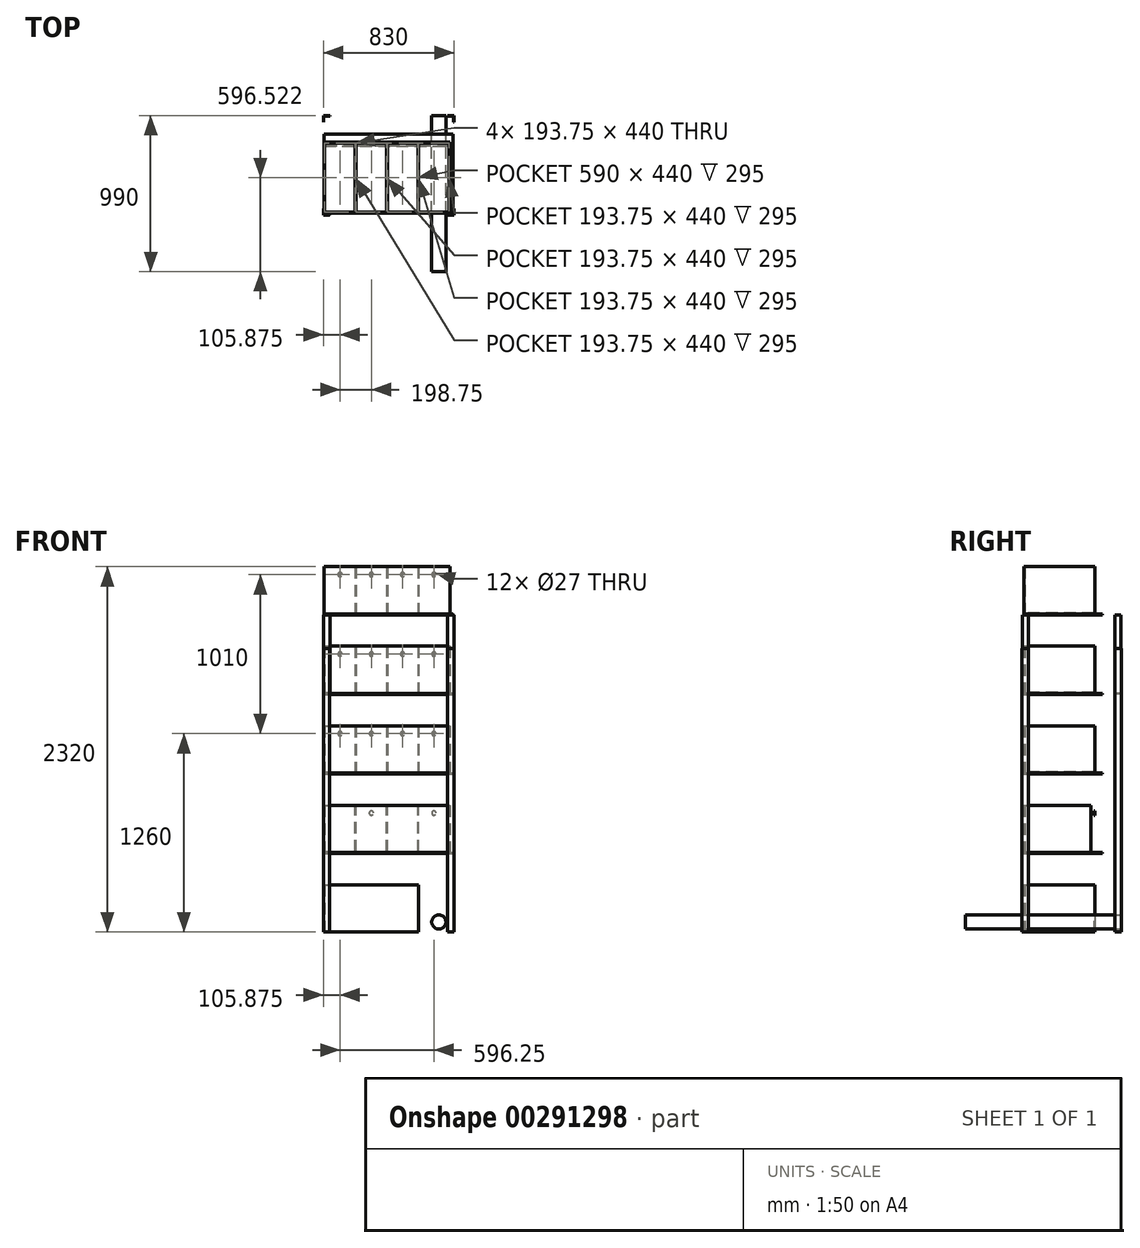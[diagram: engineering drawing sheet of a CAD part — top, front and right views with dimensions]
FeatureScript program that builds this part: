
annotation { "Feature Type Name" : "Feature", "Feature Type Description" : "" }
export const myFeature = defineFeature(function(context is Context, id is Id, definition is map)
    precondition{}
    {
        {
            var Q0;
            Q0=qCreatedBy(makeId("Top.planeOp"),FACE);
            var sketch = newSketch(context, id + "F0", { "sketchPlane" : qUnion([Q0])});
            skLineSegment(sketch, "E0.bottom", {"start": v(-415, 315) * mm, "end": v(415, 315) * mm});
            skLineSegment(sketch, "E0.top", {"start": v(-415, -315) * mm, "end": v(415, -315) * mm});
            skLineSegment(sketch, "E0.left", {"start": v(-415, 315) * mm, "end": v(-415, -315) * mm});
            skLineSegment(sketch, "E0.right", {"start": v(415, 315) * mm, "end": v(415, -315) * mm});
            skPoint(sketch, "E0.middle", {"position": v(0, 0) * mm});
            skSolve(sketch);
        }
        {
            var Q0;
            Q0=qCreatedBy(makeId("Top.planeOp"),FACE);
            var sketch = newSketch(context, id + "F1", { "sketchPlane" : qUnion([Q0])});
            skLineSegment(sketch, "E1.bottom", {"start": v(-411, -303.48) * mm, "end": v(409, -303.48) * mm});
            skLineSegment(sketch, "E1.top", {"start": v(-411, 196.52) * mm, "end": v(409, 196.52) * mm});
            skLineSegment(sketch, "E1.left", {"start": v(-411, -303.48) * mm, "end": v(-411, 196.52) * mm});
            skLineSegment(sketch, "E1.right", {"start": v(409, -303.48) * mm, "end": v(409, 196.52) * mm});
            skSolve(sketch);
        }
        {
            var Q0;
            Q0=qCreatedBy(makeId("Top.planeOp"),FACE);
            var sketch = newSketch(context, id + "F2", { "sketchPlane" : qUnion([Q0])});
            skPoint(sketch, "E2.0", {"position": v(-411, -303.48) * mm});
            skLineSegment(sketch, "E3.bottom", {"start": v(-411, -303.48) * mm, "end": v(189, -303.48) * mm});
            skLineSegment(sketch, "E3.top", {"start": v(-411, 146.52) * mm, "end": v(189, 146.52) * mm});
            skLineSegment(sketch, "E3.left", {"start": v(-411, -303.48) * mm, "end": v(-411, 146.52) * mm});
            skLineSegment(sketch, "E3.right", {"start": v(189, -303.48) * mm, "end": v(189, 146.52) * mm});
            skSolve(sketch);
        }
        {
            var Q0;
            Q0 = qSketchRegion(id + "F2", true);
            extrude(context, id + "F3", {"entities" : qUnion([Q0]), "depth" : 300 * mm});
        }
        {
            var Q0;
            Q0=qCreatedBy(makeId("Top.planeOp"),FACE);
            cPlane(context, id + "F4", {"entities" : qUnion([Q0]), "cplaneType" : CPlaneType.OFFSET, "offset" : 500 * mm, "width" : 150 * mm, "height" : 150 * mm});
        }
        {
            var Q0;
            Q0=qCreatedBy(id+"F4.planeOp",FACE);
            var sketch = newSketch(context, id + "F5", { "sketchPlane" : qUnion([Q0])});
            skLineSegment(sketch, "E4.0", {"start": v(-411, 196.52) * mm, "end": v(409, 196.52) * mm});
            skLineSegment(sketch, "E5.0", {"start": v(-411, -303.48) * mm, "end": v(-411, 196.52) * mm});
            skPoint(sketch, "E6.0", {"position": v(409, -303.48) * mm});
            skLineSegment(sketch, "E7.top", {"start": v(-411, -303.48) * mm, "end": v(409, -303.48) * mm});
            skLineSegment(sketch, "E7.left", {"start": v(-411, 196.52) * mm, "end": v(-411, -303.48) * mm});
            skLineSegment(sketch, "E7.right", {"start": v(409, 196.52) * mm, "end": v(409, -303.48) * mm});
            skSolve(sketch);
        }
        {
            var Q0;
            Q0 = qSketchRegion(id + "F5", true);
            extrude(context, id + "F6", {"entities" : qUnion([Q0]), "depth" : 5 * mm});
        }
        {
            var Q0;
            Q0=makeQuery(id+"F6.opExtrude","CAP_FACE",FACE,{"disambiguationData":[OSD([sQuery(id+"F5.wireOp",EDGE,"E4.0"),sQuery(id+"F5.wireOp",EDGE,"E7.top"),sQuery(id+"F5.wireOp",EDGE,"E7.left"),sQuery(id+"F5.wireOp",EDGE,"E7.right")])],"isStart":false});
            var sketch = newSketch(context, id + "F7", { "sketchPlane" : qUnion([Q0])});
            skPoint(sketch, "E8.0", {"position": v(-411, -303.48) * mm});
            skLineSegment(sketch, "E9.bottom", {"start": v(-411, -303.48) * mm, "end": v(389, -303.48) * mm});
            skLineSegment(sketch, "E9.top", {"start": v(-411, 146.52) * mm, "end": v(389, 146.52) * mm});
            skLineSegment(sketch, "E9.left", {"start": v(-411, -303.48) * mm, "end": v(-411, 146.52) * mm});
            skLineSegment(sketch, "E9.right", {"start": v(389, -303.48) * mm, "end": v(389, 146.52) * mm});
            skSolve(sketch);
        }
        {
            var Q0;
            Q0=makeQuery(id+"F7.imprint","IMPRINT",FACE,{"disambiguationData":[TD([[makeQuery(id+"F7.imprint","IMPRINT",EDGE,{"derivedFrom":sQuery(id+"F7.wireOp",EDGE,"E9.bottom")}),1.0]])]});
            extrude(context, id + "F8", {"entities" : qUnion([Q0]), "depth" : 300 * mm});
        }
        {
            var Q0;
            Q0=makeQuery(id+"F8.opExtrude","CAP_FACE",FACE,{"disambiguationData":[OSD([sQuery(id+"F7.wireOp",EDGE,"E9.bottom"),sQuery(id+"F7.wireOp",EDGE,"E9.top"),sQuery(id+"F7.wireOp",EDGE,"E9.left"),sQuery(id+"F7.wireOp",EDGE,"E9.right")])],"isStart":false});
            shell(context, id + "F9", {"entities" : qUnion([Q0]), "thickness" : 5 * mm});
        }
        {
            var Q0;
            Q0=makeQuery(id+"F6.opExtrude","CAP_FACE",FACE,{"disambiguationData":[OSD([sQuery(id+"F5.wireOp",EDGE,"E4.0"),sQuery(id+"F5.wireOp",EDGE,"E7.top"),sQuery(id+"F5.wireOp",EDGE,"E7.left"),sQuery(id+"F5.wireOp",EDGE,"E7.right")])],"isStart":false});
            cPlane(context, id + "F10", {"entities" : qUnion([Q0]), "cplaneType" : CPlaneType.OFFSET, "offset" : 500 * mm, "width" : 150 * mm, "height" : 150 * mm});
        }
        {
            var Q0;
            Q0=qCreatedBy(id+"F10.planeOp",FACE);
            var sketch = newSketch(context, id + "F11", { "sketchPlane" : qUnion([Q0])});
            skPoint(sketch, "E10.0", {"position": v(-411, -303.48) * mm});
            skPoint(sketch, "E11.0", {"position": v(409, 196.52) * mm});
            skLineSegment(sketch, "E12.bottom", {"start": v(-411, -303.48) * mm, "end": v(409, -303.48) * mm});
            skLineSegment(sketch, "E12.top", {"start": v(-411, 196.52) * mm, "end": v(409, 196.52) * mm});
            skLineSegment(sketch, "E12.left", {"start": v(-411, -303.48) * mm, "end": v(-411, 196.52) * mm});
            skLineSegment(sketch, "E12.right", {"start": v(409, -303.48) * mm, "end": v(409, 196.52) * mm});
            skSolve(sketch);
        }
        {
            var Q0;
            Q0 = qSketchRegion(id + "F11", true);
            extrude(context, id + "F12", {"entities" : qUnion([Q0]), "depth" : 5 * mm});
        }
        {
            var Q0;
            Q0=makeQuery(id+"F12.opExtrude","CAP_FACE",FACE,{"disambiguationData":[OSD([sQuery(id+"F11.wireOp",EDGE,"E12.bottom"),sQuery(id+"F11.wireOp",EDGE,"E12.top"),sQuery(id+"F11.wireOp",EDGE,"E12.left"),sQuery(id+"F11.wireOp",EDGE,"E12.right")])],"isStart":false});
            var sketch = newSketch(context, id + "F13", { "sketchPlane" : qUnion([Q0])});
            skPoint(sketch, "E13.0", {"position": v(-411, -303.48) * mm});
            skLineSegment(sketch, "E14.bottom", {"start": v(-411, -303.48) * mm, "end": v(389, -303.48) * mm});
            skLineSegment(sketch, "E14.top", {"start": v(-411, 146.52) * mm, "end": v(389, 146.52) * mm});
            skLineSegment(sketch, "E14.left", {"start": v(-411, -303.48) * mm, "end": v(-411, 146.52) * mm});
            skLineSegment(sketch, "E14.right", {"start": v(389, -303.48) * mm, "end": v(389, 146.52) * mm});
            skSolve(sketch);
        }
        {
            var Q0;
            Q0=makeQuery(id+"F13.imprint","IMPRINT",FACE,{"disambiguationData":[TD([[makeQuery(id+"F13.imprint","IMPRINT",EDGE,{"derivedFrom":sQuery(id+"F13.wireOp",EDGE,"E14.bottom")}),1.0]])]});
            extrude(context, id + "F14", {"entities" : qUnion([Q0]), "depth" : 300 * mm});
        }
        {
            var Q0;
            Q0=makeQuery(id+"F14.opExtrude","CAP_FACE",FACE,{"disambiguationData":[OSD([sQuery(id+"F13.wireOp",EDGE,"E14.bottom"),sQuery(id+"F13.wireOp",EDGE,"E14.top"),sQuery(id+"F13.wireOp",EDGE,"E14.left"),sQuery(id+"F13.wireOp",EDGE,"E14.right")])],"isStart":false});
            shell(context, id + "F15", {"entities" : qUnion([Q0]), "thickness" : 5 * mm});
        }
        {
            var Q0;
            Q0=makeQuery(id+"F12.opExtrude","CAP_FACE",FACE,{"disambiguationData":[OSD([sQuery(id+"F11.wireOp",EDGE,"E12.bottom"),sQuery(id+"F11.wireOp",EDGE,"E12.top"),sQuery(id+"F11.wireOp",EDGE,"E12.left"),sQuery(id+"F11.wireOp",EDGE,"E12.right")])],"isStart":false});
            cPlane(context, id + "F16", {"entities" : qUnion([Q0]), "cplaneType" : CPlaneType.OFFSET, "offset" : 500 * mm, "width" : 150 * mm, "height" : 150 * mm});
        }
        {
            var Q0;
            Q0=qCreatedBy(id+"F16.planeOp",FACE);
            var sketch = newSketch(context, id + "F17", { "sketchPlane" : qUnion([Q0])});
            skPoint(sketch, "E15.0", {"position": v(-411, -303.48) * mm});
            skPoint(sketch, "E16.0", {"position": v(409, 196.52) * mm});
            skLineSegment(sketch, "E17.bottom", {"start": v(-411, -303.48) * mm, "end": v(409, -303.48) * mm});
            skLineSegment(sketch, "E17.top", {"start": v(-411, 196.52) * mm, "end": v(409, 196.52) * mm});
            skLineSegment(sketch, "E17.left", {"start": v(-411, -303.48) * mm, "end": v(-411, 196.52) * mm});
            skLineSegment(sketch, "E17.right", {"start": v(409, -303.48) * mm, "end": v(409, 196.52) * mm});
            skSolve(sketch);
        }
        {
            var Q0;
            Q0 = qSketchRegion(id + "F17", true);
            extrude(context, id + "F18", {"entities" : qUnion([Q0]), "depth" : 5 * mm});
        }
        {
            var Q0;
            Q0=makeQuery(id+"F18.opExtrude","CAP_FACE",FACE,{"disambiguationData":[OSD([sQuery(id+"F17.wireOp",EDGE,"E17.bottom"),sQuery(id+"F17.wireOp",EDGE,"E17.top"),sQuery(id+"F17.wireOp",EDGE,"E17.left"),sQuery(id+"F17.wireOp",EDGE,"E17.right")])],"isStart":false});
            var sketch = newSketch(context, id + "F19", { "sketchPlane" : qUnion([Q0])});
            skPoint(sketch, "E18.0", {"position": v(-411, -303.48) * mm});
            skLineSegment(sketch, "E19.bottom", {"start": v(-411, -303.48) * mm, "end": v(389, -303.48) * mm});
            skLineSegment(sketch, "E19.top", {"start": v(-411, 146.52) * mm, "end": v(389, 146.52) * mm});
            skLineSegment(sketch, "E19.left", {"start": v(-411, -303.48) * mm, "end": v(-411, 146.52) * mm});
            skLineSegment(sketch, "E19.right", {"start": v(389, -303.48) * mm, "end": v(389, 146.52) * mm});
            skSolve(sketch);
        }
        {
            var Q0;
            Q0=makeQuery(id+"F19.imprint","IMPRINT",FACE,{"disambiguationData":[TD([[makeQuery(id+"F19.imprint","IMPRINT",EDGE,{"derivedFrom":sQuery(id+"F19.wireOp",EDGE,"E19.bottom")}),1.0]])]});
            extrude(context, id + "F20", {"entities" : qUnion([Q0]), "depth" : 300 * mm});
        }
        {
            var Q0;
            Q0=makeQuery(id+"F20.opExtrude","CAP_FACE",FACE,{"disambiguationData":[OSD([sQuery(id+"F19.wireOp",EDGE,"E19.bottom"),sQuery(id+"F19.wireOp",EDGE,"E19.top"),sQuery(id+"F19.wireOp",EDGE,"E19.left"),sQuery(id+"F19.wireOp",EDGE,"E19.right")])],"isStart":false});
            shell(context, id + "F21", {"entities" : qUnion([Q0]), "thickness" : 5 * mm});
        }
        {
            var Q0;
            Q0=makeQuery(id+"F18.opExtrude","CAP_FACE",FACE,{"disambiguationData":[OSD([sQuery(id+"F17.wireOp",EDGE,"E17.bottom"),sQuery(id+"F17.wireOp",EDGE,"E17.top"),sQuery(id+"F17.wireOp",EDGE,"E17.left"),sQuery(id+"F17.wireOp",EDGE,"E17.right")])],"isStart":false});
            cPlane(context, id + "F22", {"entities" : qUnion([Q0]), "cplaneType" : CPlaneType.OFFSET, "offset" : 500 * mm, "width" : 150 * mm, "height" : 150 * mm});
        }
        {
            var Q0;
            Q0=qCreatedBy(id+"F22.planeOp",FACE);
            var sketch = newSketch(context, id + "F23", { "sketchPlane" : qUnion([Q0])});
            skPoint(sketch, "E20.0", {"position": v(-411, -303.48) * mm});
            skPoint(sketch, "E21.0", {"position": v(409, 196.52) * mm});
            skLineSegment(sketch, "E22.bottom", {"start": v(-411, -303.48) * mm, "end": v(409, -303.48) * mm});
            skLineSegment(sketch, "E22.top", {"start": v(-411, 196.52) * mm, "end": v(409, 196.52) * mm});
            skLineSegment(sketch, "E22.left", {"start": v(-411, -303.48) * mm, "end": v(-411, 196.52) * mm});
            skLineSegment(sketch, "E22.right", {"start": v(409, -303.48) * mm, "end": v(409, 196.52) * mm});
            skSolve(sketch);
        }
        {
            var Q0;
            Q0=makeQuery(id+"F23.imprint","IMPRINT",FACE,{"disambiguationData":[TD([[makeQuery(id+"F23.imprint","IMPRINT",EDGE,{"derivedFrom":sQuery(id+"F23.wireOp",EDGE,"E22.bottom")}),1.0]])]});
            extrude(context, id + "F24", {"entities" : qUnion([Q0]), "depth" : 5 * mm});
        }
        {
            var Q0;
            Q0=makeQuery(id+"F24.opExtrude","CAP_FACE",FACE,{"disambiguationData":[OSD([sQuery(id+"F23.wireOp",EDGE,"E22.bottom"),sQuery(id+"F23.wireOp",EDGE,"E22.top"),sQuery(id+"F23.wireOp",EDGE,"E22.left"),sQuery(id+"F23.wireOp",EDGE,"E22.right")])],"isStart":false});
            var sketch = newSketch(context, id + "F25", { "sketchPlane" : qUnion([Q0])});
            skPoint(sketch, "E23.0", {"position": v(-411, -303.48) * mm});
            skLineSegment(sketch, "E24.bottom", {"start": v(-411, -303.48) * mm, "end": v(389, -303.48) * mm});
            skLineSegment(sketch, "E24.top", {"start": v(-411, 146.52) * mm, "end": v(389, 146.52) * mm});
            skLineSegment(sketch, "E24.left", {"start": v(-411, -303.48) * mm, "end": v(-411, 146.52) * mm});
            skLineSegment(sketch, "E24.right", {"start": v(389, -303.48) * mm, "end": v(389, 146.52) * mm});
            skSolve(sketch);
        }
        {
            var Q0;
            Q0=makeQuery(id+"F25.imprint","IMPRINT",FACE,{"disambiguationData":[TD([[makeQuery(id+"F25.imprint","IMPRINT",EDGE,{"derivedFrom":sQuery(id+"F25.wireOp",EDGE,"E24.bottom")}),1.0]])]});
            extrude(context, id + "F26", {"entities" : qUnion([Q0]), "depth" : 300 * mm});
        }
        {
            var Q0;
            Q0=makeQuery(id+"F26.opExtrude","CAP_FACE",FACE,{"disambiguationData":[OSD([sQuery(id+"F25.wireOp",EDGE,"E24.bottom"),sQuery(id+"F25.wireOp",EDGE,"E24.top"),sQuery(id+"F25.wireOp",EDGE,"E24.left"),sQuery(id+"F25.wireOp",EDGE,"E24.right")])],"isStart":false});
            shell(context, id + "F27", {"entities" : qUnion([Q0]), "thickness" : 5 * mm});
        }
        {
            var Q0;
            Q0=sQuery(id+"F0.wireOp",EDGE,"E0.bottom");
            var Q1;
            Q1=makeQuery(id+"F1.imprint","IMPRINT",FACE,{"disambiguationData":[TD([[makeQuery(id+"F1.imprint","IMPRINT",EDGE,{"derivedFrom":sQuery(id+"F1.wireOp",EDGE,"E1.bottom")}),1.0]])]});
            cPlane(context, id + "F28", {"entities" : qUnion([Q0, Q1]), "cplaneType" : CPlaneType.LINE_ANGLE, "offset" : 25 * mm, "angle" : 90 * degree, "oppositeDirection" : true, "width" : 150 * mm, "height" : 150 * mm});
        }
        {
            var Q0;
            Q0=qCreatedBy(id+"F28.planeOp",FACE);
            var sketch = newSketch(context, id + "F29", { "sketchPlane" : qUnion([Q0])});
            skCircle(sketch, "E25", {"center": v(318.2, 63.11) * mm, "radius": 45 * mm});
            skSolve(sketch);
        }
        {
            var Q0;
            Q0=makeQuery(id+"F29.imprint","IMPRINT",FACE,{"disambiguationData":[TD([[makeQuery(id+"F29.imprint","IMPRINT",EDGE,{"derivedFrom":sQuery(id+"F29.wireOp",EDGE,"E25")}),1.0]])]});
            extrude(context, id + "F30", {"entities" : qUnion([Q0]), "depth" : 990 * mm});
        }
        {
            var Q0;
            Q0=makeQuery(id+"F9.opShell","OFFSET_FACE",FACE,{"disambiguationData":[OSD([sQuery(id+"F7.wireOp",EDGE,"E9.bottom"),sQuery(id+"F7.wireOp",EDGE,"E9.top"),sQuery(id+"F7.wireOp",EDGE,"E9.left"),sQuery(id+"F7.wireOp",EDGE,"E9.right")])]});
            var sketch = newSketch(context, id + "F31", { "sketchPlane" : qUnion([Q0])});
            skLineSegment(sketch, "E26.0.0", {"start": v(384, 141.52) * mm, "end": v(-406, 141.52) * mm});
            skLineSegment(sketch, "E26.0.1", {"start": v(-406, 141.52) * mm, "end": v(-406, -298.48) * mm});
            skLineSegment(sketch, "E26.0.2", {"start": v(-406, -298.48) * mm, "end": v(384, -298.48) * mm});
            skLineSegment(sketch, "E26.0.3", {"start": v(384, -298.48) * mm, "end": v(384, 141.52) * mm});
            skPoint(sketch, "E27", {"position": v(-11, -298.48) * mm});
            skPoint(sketch, "E28", {"position": v(-11, 141.52) * mm});
            skLineSegment(sketch, "E29", {"start": v(-11, 141.52) * mm, "end": v(-11, -298.48) * mm});
            skLineSegment(sketch, "E30", {"start": v(-406, 141.52) * mm, "end": v(-11, 141.52) * mm});
            skLineSegment(sketch, "E31", {"start": v(-11, 141.52) * mm, "end": v(384, 141.52) * mm});
            skLineSegment(sketch, "E32", {"start": v(-13.5, 141.52) * mm, "end": v(-13.5, -298.48) * mm});
            skLineSegment(sketch, "E33.MirrorCS", {"start": v(-8.5, 141.52) * mm, "end": v(-8.5, -298.48) * mm});
            skLineSegment(sketch, "E34.0", {"start": v(-411, -303.48) * mm, "end": v(-411, 196.52) * mm});
            skLineSegment(sketch, "E35", {"start": v(-11, 141.52) * mm, "end": v(-411, 141.52) * mm});
            skPoint(sketch, "E36", {"position": v(-408.5, 159.68) * mm});
            skPoint(sketch, "E37.orphan", {"position": v(-411, 159.68) * mm});
            skPoint(sketch, "E38", {"position": v(-209.75, 141.52) * mm});
            skLineSegment(sketch, "E39", {"start": v(-209.75, 141.52) * mm, "end": v(-209.75, -298.48) * mm});
            skLineSegment(sketch, "E40", {"start": v(-212.25, 141.52) * mm, "end": v(-212.25, -298.48) * mm});
            skLineSegment(sketch, "E41.MirrorCS", {"start": v(-207.25, 141.52) * mm, "end": v(-207.25, -298.48) * mm});
            skLineSegment(sketch, "E42.MirrorCS", {"start": v(185.25, 141.52) * mm, "end": v(185.25, -298.48) * mm});
            skLineSegment(sketch, "E43.MirrorCS", {"start": v(190.25, 141.52) * mm, "end": v(190.25, -298.48) * mm});
            skLineSegment(sketch, "E44", {"start": v(185.25, 141.52) * mm, "end": v(190.25, 141.52) * mm});
            skLineSegment(sketch, "E45", {"start": v(185.25, -298.48) * mm, "end": v(190.25, -298.48) * mm});
            skLineSegment(sketch, "E46", {"start": v(-13.5, 151.47) * mm, "end": v(-406, 151.47) * mm});
            skPoint(sketch, "E47", {"position": v(-209.75, 151.47) * mm});
            skSolve(sketch);
        }
        {
            var Q0;
            {var subQ0=sQuery(id+"F31.wireOp",EDGE,"E39");Q0=makeQuery(id+"F31.imprint","IMPRINT",FACE,{"disambiguationData":[TD([[makeQuery(id+"F31.imprint","IMPRINT",EDGE,{"derivedFrom":subQ0}),-1.0]])]});}
            var Q1;
            {var subQ0=sQuery(id+"F31.wireOp",EDGE,"E39");Q1=makeQuery(id+"F31.imprint","IMPRINT",FACE,{"disambiguationData":[TD([[makeQuery(id+"F31.imprint","IMPRINT",EDGE,{"derivedFrom":subQ0}),1.0]])]});}
            var Q2;
            {var subQ0=sQuery(id+"F31.wireOp",EDGE,"E29");Q2=makeQuery(id+"F31.imprint","IMPRINT",FACE,{"disambiguationData":[TD([[makeQuery(id+"F31.imprint","IMPRINT",EDGE,{"derivedFrom":subQ0}),-1.0]])]});}
            var Q3;
            {var subQ0=sQuery(id+"F31.wireOp",EDGE,"E29");Q3=makeQuery(id+"F31.imprint","IMPRINT",FACE,{"disambiguationData":[TD([[makeQuery(id+"F31.imprint","IMPRINT",EDGE,{"derivedFrom":subQ0}),1.0]])]});}
            var Q4;
            Q4=makeQuery(id+"F31.imprint","IMPRINT",FACE,{"disambiguationData":[TD([[makeQuery(id+"F31.imprint","IMPRINT",EDGE,{"derivedFrom":sQuery(id+"F31.wireOp",EDGE,"E42.MirrorCS")}),1.0]])]});
            var Q5;
            Q5=makeQuery(id+"F8.opExtrude","CAP_FACE",FACE,{"disambiguationData":[OSD([sQuery(id+"F7.wireOp",EDGE,"E9.bottom"),sQuery(id+"F7.wireOp",EDGE,"E9.top"),sQuery(id+"F7.wireOp",EDGE,"E9.left"),sQuery(id+"F7.wireOp",EDGE,"E9.right")])],"isStart":false});
            extrude(context, id + "F32", {"entities" : qUnion([Q0, Q1, Q2, Q3, Q4]), "operationType" : NewBodyOperationType.ADD, "endBound" : BoundingType.UP_TO_SURFACE, "endBoundEntityFace" : qUnion([Q5]), "depth" : 26 * mm});
        }
        {
            var Q0;
            Q0=makeQuery(id+"F15.opShell","OFFSET_FACE",FACE,{"disambiguationData":[OSD([sQuery(id+"F13.wireOp",EDGE,"E14.bottom"),sQuery(id+"F13.wireOp",EDGE,"E14.top"),sQuery(id+"F13.wireOp",EDGE,"E14.left"),sQuery(id+"F13.wireOp",EDGE,"E14.right")])]});
            var sketch = newSketch(context, id + "F33", { "sketchPlane" : qUnion([Q0])});
            skLineSegment(sketch, "E48.0", {"start": v(-13.5, 141.52) * mm, "end": v(-13.5, -298.48) * mm});
            skLineSegment(sketch, "E49.0", {"start": v(-8.5, 141.52) * mm, "end": v(-8.5, -298.48) * mm});
            skLineSegment(sketch, "E50.0", {"start": v(185.25, 141.52) * mm, "end": v(185.25, -298.48) * mm});
            skLineSegment(sketch, "E51.0", {"start": v(190.25, 141.52) * mm, "end": v(190.25, -298.48) * mm});
            skLineSegment(sketch, "E52.0", {"start": v(-207.25, 141.52) * mm, "end": v(-207.25, -298.48) * mm});
            skLineSegment(sketch, "E53.0", {"start": v(-212.25, 141.52) * mm, "end": v(-212.25, -298.48) * mm});
            skSolve(sketch);
        }
        {
            var Q0;
            {var subQ0=sQuery(id+"F33.wireOp",EDGE,"E52.0");Q0=makeQuery(id+"F33.imprint","IMPRINT",FACE,{"disambiguationData":[TD([[makeQuery(id+"F33.imprint","IMPRINT",EDGE,{"derivedFrom":subQ0}),-1.0]])]});}
            var Q1;
            {var subQ0=sQuery(id+"F33.wireOp",EDGE,"E48.0");Q1=makeQuery(id+"F33.imprint","IMPRINT",FACE,{"disambiguationData":[TD([[makeQuery(id+"F33.imprint","IMPRINT",EDGE,{"derivedFrom":subQ0}),1.0]])]});}
            var Q2;
            {var subQ0=sQuery(id+"F33.wireOp",EDGE,"E50.0");Q2=makeQuery(id+"F33.imprint","IMPRINT",FACE,{"disambiguationData":[TD([[makeQuery(id+"F33.imprint","IMPRINT",EDGE,{"derivedFrom":subQ0}),1.0]])]});}
            var Q3;
            Q3=makeQuery(id+"F14.opExtrude","CAP_FACE",FACE,{"disambiguationData":[OSD([sQuery(id+"F13.wireOp",EDGE,"E14.bottom"),sQuery(id+"F13.wireOp",EDGE,"E14.top"),sQuery(id+"F13.wireOp",EDGE,"E14.left"),sQuery(id+"F13.wireOp",EDGE,"E14.right")])],"isStart":false});
            extrude(context, id + "F34", {"entities" : qUnion([Q0, Q1, Q2]), "operationType" : NewBodyOperationType.ADD, "endBound" : BoundingType.UP_TO_SURFACE, "endBoundEntityFace" : qUnion([Q3]), "depth" : 25 * mm});
        }
        {
            var Q0;
            Q0=makeQuery(id+"F21.opShell","OFFSET_FACE",FACE,{"disambiguationData":[OSD([sQuery(id+"F19.wireOp",EDGE,"E19.bottom"),sQuery(id+"F19.wireOp",EDGE,"E19.top"),sQuery(id+"F19.wireOp",EDGE,"E19.left"),sQuery(id+"F19.wireOp",EDGE,"E19.right")])]});
            var sketch = newSketch(context, id + "F35", { "sketchPlane" : qUnion([Q0])});
            skLineSegment(sketch, "E54.0", {"start": v(-8.5, 141.52) * mm, "end": v(-8.5, -298.48) * mm});
            skLineSegment(sketch, "E55.0", {"start": v(-13.5, 141.52) * mm, "end": v(-13.5, -298.48) * mm});
            skLineSegment(sketch, "E56.0", {"start": v(-207.25, 141.52) * mm, "end": v(-207.25, -298.48) * mm});
            skLineSegment(sketch, "E57.0", {"start": v(-212.25, 141.52) * mm, "end": v(-212.25, -298.48) * mm});
            skLineSegment(sketch, "E58.0", {"start": v(185.25, 141.52) * mm, "end": v(185.25, -298.48) * mm});
            skLineSegment(sketch, "E59.0", {"start": v(190.25, 141.52) * mm, "end": v(190.25, -298.48) * mm});
            skSolve(sketch);
        }
        {
            var Q0;
            {var subQ0=sQuery(id+"F35.wireOp",EDGE,"E56.0");Q0=makeQuery(id+"F35.imprint","IMPRINT",FACE,{"disambiguationData":[TD([[makeQuery(id+"F35.imprint","IMPRINT",EDGE,{"derivedFrom":subQ0}),-1.0]])]});}
            var Q1;
            {var subQ0=sQuery(id+"F35.wireOp",EDGE,"E54.0");Q1=makeQuery(id+"F35.imprint","IMPRINT",FACE,{"disambiguationData":[TD([[makeQuery(id+"F35.imprint","IMPRINT",EDGE,{"derivedFrom":subQ0}),-1.0]])]});}
            var Q2;
            {var subQ0=sQuery(id+"F35.wireOp",EDGE,"E58.0");Q2=makeQuery(id+"F35.imprint","IMPRINT",FACE,{"disambiguationData":[TD([[makeQuery(id+"F35.imprint","IMPRINT",EDGE,{"derivedFrom":subQ0}),1.0]])]});}
            var Q3;
            Q3=makeQuery(id+"F20.opExtrude","CAP_FACE",FACE,{"disambiguationData":[OSD([sQuery(id+"F19.wireOp",EDGE,"E19.bottom"),sQuery(id+"F19.wireOp",EDGE,"E19.top"),sQuery(id+"F19.wireOp",EDGE,"E19.left"),sQuery(id+"F19.wireOp",EDGE,"E19.right")])],"isStart":false});
            extrude(context, id + "F36", {"entities" : qUnion([Q0, Q1, Q2]), "operationType" : NewBodyOperationType.ADD, "endBound" : BoundingType.UP_TO_SURFACE, "endBoundEntityFace" : qUnion([Q3]), "depth" : 25 * mm});
        }
        {
            var Q0;
            Q0=makeQuery(id+"F27.opShell","OFFSET_FACE",FACE,{"disambiguationData":[OSD([sQuery(id+"F25.wireOp",EDGE,"E24.bottom"),sQuery(id+"F25.wireOp",EDGE,"E24.top"),sQuery(id+"F25.wireOp",EDGE,"E24.left"),sQuery(id+"F25.wireOp",EDGE,"E24.right")])]});
            var sketch = newSketch(context, id + "F37", { "sketchPlane" : qUnion([Q0])});
            skLineSegment(sketch, "E60.0", {"start": v(-212.25, 141.52) * mm, "end": v(-212.25, -298.48) * mm});
            skLineSegment(sketch, "E61.0", {"start": v(-207.25, 141.52) * mm, "end": v(-207.25, -298.48) * mm});
            skLineSegment(sketch, "E62.0", {"start": v(-13.5, 141.52) * mm, "end": v(-13.5, -298.48) * mm});
            skLineSegment(sketch, "E63.0", {"start": v(-8.5, 141.52) * mm, "end": v(-8.5, -298.48) * mm});
            skLineSegment(sketch, "E64.0", {"start": v(185.25, 141.52) * mm, "end": v(185.25, -298.48) * mm});
            skLineSegment(sketch, "E65.0", {"start": v(190.25, 141.52) * mm, "end": v(190.25, -298.48) * mm});
            skSolve(sketch);
        }
        {
            var Q0;
            {var subQ0=sQuery(id+"F37.wireOp",EDGE,"E60.0");Q0=makeQuery(id+"F37.imprint","IMPRINT",FACE,{"disambiguationData":[TD([[makeQuery(id+"F37.imprint","IMPRINT",EDGE,{"derivedFrom":subQ0}),1.0]])]});}
            var Q1;
            {var subQ0=sQuery(id+"F37.wireOp",EDGE,"E62.0");Q1=makeQuery(id+"F37.imprint","IMPRINT",FACE,{"disambiguationData":[TD([[makeQuery(id+"F37.imprint","IMPRINT",EDGE,{"derivedFrom":subQ0}),1.0]])]});}
            var Q2;
            {var subQ0=sQuery(id+"F37.wireOp",EDGE,"E64.0");Q2=makeQuery(id+"F37.imprint","IMPRINT",FACE,{"disambiguationData":[TD([[makeQuery(id+"F37.imprint","IMPRINT",EDGE,{"derivedFrom":subQ0}),1.0]])]});}
            var Q3;
            Q3=makeQuery(id+"F26.opExtrude","CAP_FACE",FACE,{"disambiguationData":[OSD([sQuery(id+"F25.wireOp",EDGE,"E24.bottom"),sQuery(id+"F25.wireOp",EDGE,"E24.top"),sQuery(id+"F25.wireOp",EDGE,"E24.left"),sQuery(id+"F25.wireOp",EDGE,"E24.right")])],"isStart":false});
            extrude(context, id + "F38", {"entities" : qUnion([Q0, Q1, Q2]), "operationType" : NewBodyOperationType.ADD, "endBound" : BoundingType.UP_TO_SURFACE, "endBoundEntityFace" : qUnion([Q3]), "depth" : 25 * mm});
        }
        {
            var Q0;
            Q0=qCreatedBy(makeId("Top.planeOp"),FACE);
            var sketch = newSketch(context, id + "F39", { "sketchPlane" : qUnion([Q0])});
            skLineSegment(sketch, "E66.0", {"start": v(-415, -315) * mm, "end": v(415, -315) * mm});
            skLineSegment(sketch, "E67.0", {"start": v(-415, 315) * mm, "end": v(-415, -315) * mm});
            skLineSegment(sketch, "E68", {"start": v(-415, -275) * mm, "end": v(-414, -275) * mm});
            skLineSegment(sketch, "E69", {"start": v(-414, -275) * mm, "end": v(-414, -314) * mm});
            skLineSegment(sketch, "E70", {"start": v(-414, -314) * mm, "end": v(-375, -314) * mm});
            skLineSegment(sketch, "E71", {"start": v(-375, -314) * mm, "end": v(-375, -315) * mm});
            skLineSegment(sketch, "E72", {"start": v(375, -315) * mm, "end": v(375, -314) * mm});
            skLineSegment(sketch, "E73", {"start": v(375, -314) * mm, "end": v(414, -314) * mm});
            skLineSegment(sketch, "E74", {"start": v(414, -314) * mm, "end": v(414, -275) * mm});
            skLineSegment(sketch, "E75", {"start": v(414, -275) * mm, "end": v(415, -275) * mm});
            skLineSegment(sketch, "E76", {"start": v(415, -275) * mm, "end": v(415, -315) * mm});
            skLineSegment(sketch, "E77", {"start": v(-415, 275) * mm, "end": v(-414, 275) * mm});
            skLineSegment(sketch, "E78", {"start": v(-414, 275) * mm, "end": v(-414, 314) * mm});
            skLineSegment(sketch, "E79", {"start": v(-414, 314) * mm, "end": v(-375, 314) * mm});
            skLineSegment(sketch, "E80", {"start": v(-375, 314) * mm, "end": v(-375, 315) * mm});
            skLineSegment(sketch, "E81", {"start": v(-375, 315) * mm, "end": v(-415, 315) * mm});
            skLineSegment(sketch, "E82", {"start": v(375, 315) * mm, "end": v(415, 315) * mm});
            skLineSegment(sketch, "E83", {"start": v(415, 315) * mm, "end": v(415, 275) * mm});
            skLineSegment(sketch, "E84", {"start": v(415, 275) * mm, "end": v(414, 275) * mm});
            skLineSegment(sketch, "E85", {"start": v(414, 275) * mm, "end": v(414, 314) * mm});
            skLineSegment(sketch, "E86", {"start": v(414, 314) * mm, "end": v(375, 314) * mm});
            skLineSegment(sketch, "E87", {"start": v(375, 314) * mm, "end": v(375, 315) * mm});
            skSolve(sketch);
        }
        {
            var Q0;
            {var subQ0=sQuery(id+"F39.wireOp",EDGE,"E68");Q0=makeQuery(id+"F39.imprint","IMPRINT",FACE,{"disambiguationData":[TD([[makeQuery(id+"F39.imprint","IMPRINT",EDGE,{"derivedFrom":subQ0}),-1.0]])]});}
            var Q1;
            {var subQ0=sQuery(id+"F39.wireOp",EDGE,"E72");Q1=makeQuery(id+"F39.imprint","IMPRINT",FACE,{"disambiguationData":[TD([[makeQuery(id+"F39.imprint","IMPRINT",EDGE,{"derivedFrom":subQ0}),-1.0]])]});}
            var Q2;
            Q2=makeQuery(id+"F39.imprint","IMPRINT",FACE,{"disambiguationData":[TD([[makeQuery(id+"F39.imprint","IMPRINT",EDGE,{"derivedFrom":sQuery(id+"F39.wireOp",EDGE,"E82")}),-1.0]])]});
            var Q3;
            {var subQ0=sQuery(id+"F39.wireOp",EDGE,"E77");Q3=makeQuery(id+"F39.imprint","IMPRINT",FACE,{"disambiguationData":[TD([[makeQuery(id+"F39.imprint","IMPRINT",EDGE,{"derivedFrom":subQ0}),1.0]])]});}
            extrude(context, id + "F40", {"entities" : qUnion([Q0, Q1, Q2, Q3]), "depth" : 1800 * mm});
        }
        {
            var Q0;
            Q0=makeQuery(id+"F3.opExtrude","CAP_FACE",FACE,{"disambiguationData":[OSD([sQuery(id+"F2.wireOp",EDGE,"E3.bottom"),sQuery(id+"F2.wireOp",EDGE,"E3.top"),sQuery(id+"F2.wireOp",EDGE,"E3.left"),sQuery(id+"F2.wireOp",EDGE,"E3.right")])],"isStart":false});
            shell(context, id + "F41", {"entities" : qUnion([Q0]), "thickness" : 5 * mm});
        }
        {
            var Q0;
            Q0=makeQuery(id+"F18.opExtrude","CAP_FACE",FACE,{"disambiguationData":[OSD([sQuery(id+"F17.wireOp",EDGE,"E17.bottom"),sQuery(id+"F17.wireOp",EDGE,"E17.top"),sQuery(id+"F17.wireOp",EDGE,"E17.left"),sQuery(id+"F17.wireOp",EDGE,"E17.right")])],"isStart":false});
            var sketch = newSketch(context, id + "F42", { "sketchPlane" : qUnion([Q0])});
            skLineSegment(sketch, "E88.0", {"start": v(375, -314) * mm, "end": v(414, -314) * mm});
            skLineSegment(sketch, "E89.0", {"start": v(414, -314) * mm, "end": v(414, -275) * mm});
            skLineSegment(sketch, "E90", {"start": v(414, -314) * mm, "end": v(374, -314) * mm});
            skLineSegment(sketch, "E91", {"start": v(374, -314) * mm, "end": v(374, -313) * mm});
            skLineSegment(sketch, "E92", {"start": v(374, -313) * mm, "end": v(413, -313) * mm});
            skLineSegment(sketch, "E93", {"start": v(413, -313) * mm, "end": v(413, -274) * mm});
            skLineSegment(sketch, "E94", {"start": v(413, -274) * mm, "end": v(414, -274) * mm});
            skLineSegment(sketch, "E95", {"start": v(414, -274) * mm, "end": v(414, -275) * mm});
            skLineSegment(sketch, "E96.0.0", {"start": v(-415, 315) * mm, "end": v(-415, -315) * mm});
            skLineSegment(sketch, "E96.0.1", {"start": v(-415, -315) * mm, "end": v(415, -315) * mm});
            skLineSegment(sketch, "E96.0.2", {"start": v(415, -315) * mm, "end": v(415, 315) * mm});
            skLineSegment(sketch, "E96.0.3", {"start": v(415, 315) * mm, "end": v(-415, 315) * mm});
            skLineSegment(sketch, "E97.0", {"start": v(-414, -275) * mm, "end": v(-414, -314) * mm});
            skLineSegment(sketch, "E98.0", {"start": v(-414, -314) * mm, "end": v(-375, -314) * mm});
            skLineSegment(sketch, "E99", {"start": v(-375, -314) * mm, "end": v(-374, -314) * mm});
            skLineSegment(sketch, "E100", {"start": v(-374, -314) * mm, "end": v(-374, -313) * mm});
            skLineSegment(sketch, "E101", {"start": v(-374, -313) * mm, "end": v(-413, -313) * mm});
            skLineSegment(sketch, "E102", {"start": v(-413, -313) * mm, "end": v(-413, -274) * mm});
            skLineSegment(sketch, "E103", {"start": v(-413, -274) * mm, "end": v(-414, -274) * mm});
            skLineSegment(sketch, "E104", {"start": v(-414, -274) * mm, "end": v(-414, -275) * mm});
            skLineSegment(sketch, "E105.0", {"start": v(-414, 275) * mm, "end": v(-414, 314) * mm});
            skLineSegment(sketch, "E106.0", {"start": v(-414, 314) * mm, "end": v(-375, 314) * mm});
            skLineSegment(sketch, "E107", {"start": v(-414, 275) * mm, "end": v(-414, 274) * mm});
            skLineSegment(sketch, "E108", {"start": v(-414, 274) * mm, "end": v(-413, 274) * mm});
            skLineSegment(sketch, "E109", {"start": v(-413, 274) * mm, "end": v(-413, 313) * mm});
            skLineSegment(sketch, "E110", {"start": v(-413, 313) * mm, "end": v(-374, 313) * mm});
            skLineSegment(sketch, "E111", {"start": v(-374, 313) * mm, "end": v(-374, 314) * mm});
            skLineSegment(sketch, "E112", {"start": v(-374, 314) * mm, "end": v(-375, 314) * mm});
            skLineSegment(sketch, "E113.0.0", {"start": v(-415, 315) * mm, "end": v(-415, 275) * mm});
            skLineSegment(sketch, "E113.0.1", {"start": v(-415, 275) * mm, "end": v(-414, 275) * mm});
            skLineSegment(sketch, "E113.0.4", {"start": v(-375, 314) * mm, "end": v(-375, 315) * mm});
            skLineSegment(sketch, "E113.0.5", {"start": v(-375, 315) * mm, "end": v(-415, 315) * mm});
            skLineSegment(sketch, "E114.0", {"start": v(414, 314) * mm, "end": v(375, 314) * mm});
            skLineSegment(sketch, "E115.0", {"start": v(414, 275) * mm, "end": v(414, 314) * mm});
            skLineSegment(sketch, "E116", {"start": v(375, 314) * mm, "end": v(374, 314) * mm});
            skLineSegment(sketch, "E117", {"start": v(374, 314) * mm, "end": v(374, 313) * mm});
            skLineSegment(sketch, "E118", {"start": v(374, 313) * mm, "end": v(413, 313) * mm});
            skLineSegment(sketch, "E119", {"start": v(413, 313) * mm, "end": v(413, 274) * mm});
            skLineSegment(sketch, "E120", {"start": v(413, 274) * mm, "end": v(414, 274) * mm});
            skLineSegment(sketch, "E121", {"start": v(414, 274) * mm, "end": v(414, 275) * mm});
            skSolve(sketch);
        }
        {
            var Q0;
            Q0=makeQuery(id+"F42.imprint","IMPRINT",FACE,{"disambiguationData":[TD([[makeQuery(id+"F42.imprint","IMPRINT",EDGE,{"derivedFrom":sQuery(id+"F42.wireOp",EDGE,"E114.0")}),1.0]])]});
            var Q1;
            {var subQ3=sQuery(id+"F42.wireOp",EDGE,"E89.0");Q1=makeQuery(id+"F42.imprint","IMPRINT",FACE,{"disambiguationData":[TD([[makeQuery(id+"F42.imprint","IMPRINT",EDGE,{"derivedFrom":subQ3}),1.0]])]});}
            var Q2;
            Q2=makeQuery(id+"F42.imprint","IMPRINT",FACE,{"disambiguationData":[TD([[makeQuery(id+"F42.imprint","IMPRINT",EDGE,{"derivedFrom":sQuery(id+"F42.wireOp",EDGE,"E97.0")}),1.0]])]});
            var Q3;
            Q3=makeQuery(id+"F42.imprint","IMPRINT",FACE,{"disambiguationData":[TD([[makeQuery(id+"F42.imprint","IMPRINT",EDGE,{"derivedFrom":sQuery(id+"F42.wireOp",EDGE,"E107")}),1.0]])]});
            var Q4;
            Q4=makeQuery(id+"F24.opExtrude","CAP_FACE",FACE,{"disambiguationData":[OSD([sQuery(id+"F23.wireOp",EDGE,"E22.bottom"),sQuery(id+"F23.wireOp",EDGE,"E22.top"),sQuery(id+"F23.wireOp",EDGE,"E22.left"),sQuery(id+"F23.wireOp",EDGE,"E22.right")])],"isStart":true});
            extrude(context, id + "F43", {"entities" : qUnion([Q0, Q1, Q2, Q3]), "endBound" : BoundingType.UP_TO_SURFACE, "endBoundEntityFace" : qUnion([Q4]), "depth" : 1000 * mm});
        }
        {
            var Q0;
            Q0=makeQuery(id+"F8.opExtrude","SWEPT_FACE",FACE,{"disambiguationData":[OSD([sQuery(id+"F7.wireOp",EDGE,"E9.top")])]});
            var sketch = newSketch(context, id + "F44", { "sketchPlane" : qUnion([Q0])});
            skPoint(sketch, "E122.0", {"position": v(-190.25, 805) * mm});
            skPoint(sketch, "E123.0", {"position": v(-185.25, 805) * mm});
            skLineSegment(sketch, "E124.0", {"start": v(-190.25, 805) * mm, "end": v(-190.25, 510) * mm});
            skLineSegment(sketch, "E125.0", {"start": v(-185.25, 805) * mm, "end": v(-185.25, 510) * mm});
            skLineSegment(sketch, "E126.0", {"start": v(8.5, 805) * mm, "end": v(8.5, 510) * mm});
            skLineSegment(sketch, "E127.0", {"start": v(207.25, 805) * mm, "end": v(207.25, 510) * mm});
            skLineSegment(sketch, "E128.0", {"start": v(406, 805) * mm, "end": v(406, 510) * mm});
            skLineSegment(sketch, "E129.0", {"start": v(212.25, 805) * mm, "end": v(212.25, 510) * mm});
            skLineSegment(sketch, "E130.0", {"start": v(13.5, 805) * mm, "end": v(13.5, 510) * mm});
            skLineSegment(sketch, "E131.0", {"start": v(-185.25, 1310) * mm, "end": v(-185.25, 1015) * mm});
            skLineSegment(sketch, "E132.0", {"start": v(13.5, 1310) * mm, "end": v(13.5, 1015) * mm});
            skLineSegment(sketch, "E133.0", {"start": v(212.25, 1310) * mm, "end": v(212.25, 1015) * mm});
            skLineSegment(sketch, "E134.0", {"start": v(207.25, 1310) * mm, "end": v(207.25, 1015) * mm});
            skLineSegment(sketch, "E135.0", {"start": v(406, 1310) * mm, "end": v(406, 1015) * mm});
            skLineSegment(sketch, "E136.0", {"start": v(8.5, 1310) * mm, "end": v(8.5, 1015) * mm});
            skLineSegment(sketch, "E137.0", {"start": v(-190.25, 1310) * mm, "end": v(-190.25, 1015) * mm});
            skLineSegment(sketch, "E138.0", {"start": v(-190.25, 1815) * mm, "end": v(-190.25, 1520) * mm});
            skLineSegment(sketch, "E139.0", {"start": v(8.5, 1815) * mm, "end": v(8.5, 1520) * mm});
            skLineSegment(sketch, "E140.0", {"start": v(207.25, 1815) * mm, "end": v(207.25, 1520) * mm});
            skLineSegment(sketch, "E141.0", {"start": v(-185.25, 1815) * mm, "end": v(-185.25, 1520) * mm});
            skLineSegment(sketch, "E142.0", {"start": v(13.5, 1815) * mm, "end": v(13.5, 1520) * mm});
            skLineSegment(sketch, "E143.0", {"start": v(212.25, 1815) * mm, "end": v(212.25, 1520) * mm});
            skLineSegment(sketch, "E144.0", {"start": v(-190.25, 2320) * mm, "end": v(-190.25, 2025) * mm});
            skLineSegment(sketch, "E145.0", {"start": v(8.5, 2320) * mm, "end": v(8.5, 2025) * mm});
            skLineSegment(sketch, "E146.0", {"start": v(207.25, 2320) * mm, "end": v(207.25, 2025) * mm});
            skLineSegment(sketch, "E147.0", {"start": v(406, 2320) * mm, "end": v(406, 2025) * mm});
            skLineSegment(sketch, "E148.0.0", {"start": v(8.5, 2025) * mm, "end": v(8.5, 2320) * mm});
            skLineSegment(sketch, "E149.0", {"start": v(-185.25, 2320) * mm, "end": v(-185.25, 2025) * mm});
            skLineSegment(sketch, "E150.0", {"start": v(13.5, 2320) * mm, "end": v(13.5, 2025) * mm});
            skLineSegment(sketch, "E151.0", {"start": v(212.25, 2320) * mm, "end": v(212.25, 2025) * mm});
            skLineSegment(sketch, "E152.0.0", {"start": v(-389, 2020) * mm, "end": v(411, 2020) * mm});
            skLineSegment(sketch, "E152.0.1", {"start": v(411, 2020) * mm, "end": v(411, 2320) * mm});
            skLineSegment(sketch, "E152.0.2", {"start": v(411, 2320) * mm, "end": v(-389, 2320) * mm});
            skLineSegment(sketch, "E152.0.3", {"start": v(-389, 2320) * mm, "end": v(-389, 2020) * mm});
            skLineSegment(sketch, "E153.0", {"start": v(411, 1815) * mm, "end": v(-389, 1815) * mm});
            skLineSegment(sketch, "E154.0", {"start": v(411, 1310) * mm, "end": v(-389, 1310) * mm});
            skLineSegment(sketch, "E155.0", {"start": v(411, 805) * mm, "end": v(-389, 805) * mm});
            skLineSegment(sketch, "E156", {"start": v(8.5, 805) * mm, "end": v(13.5, 805) * mm});
            skPoint(sketch, "E157", {"position": v(11, 805) * mm});
            skLineSegment(sketch, "E158", {"start": v(8.5, 805) * mm, "end": v(-185.25, 805) * mm});
            skPoint(sketch, "E159", {"position": v(-88.38, 805) * mm});
            skLineSegment(sketch, "E160", {"start": v(-88.38, 805) * mm, "end": v(-88.38, 755) * mm});
            skCircle(sketch, "E161", {"center": v(-88.38, 755) * mm, "radius": 13.5 * mm});
            skLineSegment(sketch, "E162", {"start": v(11, 805) * mm, "end": v(11, 749.4) * mm});
            skCircle(sketch, "E163.MirrorC", {"center": v(110.38, 755) * mm, "radius": 13.5 * mm});
            skLineSegment(sketch, "E164", {"start": v(-190.25, 805) * mm, "end": v(-185.25, 805) * mm});
            skLineSegment(sketch, "E165", {"start": v(-187.75, 805) * mm, "end": v(-187.75, 770.63) * mm});
            skCircle(sketch, "E166.MirrorC", {"center": v(-287.13, 755) * mm, "radius": 13.5 * mm});
            skCircle(sketch, "E167.MirrorC", {"center": v(309.13, 755) * mm, "radius": 13.5 * mm});
            skCircle(sketch, "E168", {"center": v(-88.38, 1260) * mm, "radius": 13.5 * mm});
            skCircle(sketch, "E169", {"center": v(-287.12, 1260) * mm, "radius": 13.5 * mm});
            skCircle(sketch, "E170", {"center": v(110.38, 1260) * mm, "radius": 13.5 * mm});
            skCircle(sketch, "E171", {"center": v(309.13, 1260) * mm, "radius": 13.5 * mm});
            skLineSegment(sketch, "E172.0", {"start": v(-384, 805) * mm, "end": v(-384, 510) * mm});
            skCircle(sketch, "E173", {"center": v(-287.13, 1765) * mm, "radius": 13.5 * mm});
            skCircle(sketch, "E174", {"center": v(-88.38, 1765) * mm, "radius": 13.5 * mm});
            skCircle(sketch, "E175", {"center": v(110.38, 1765) * mm, "radius": 13.5 * mm});
            skCircle(sketch, "E176", {"center": v(309.12, 1765) * mm, "radius": 13.5 * mm});
            skCircle(sketch, "E177", {"center": v(-287.13, 2270) * mm, "radius": 13.5 * mm});
            skCircle(sketch, "E178", {"center": v(-88.38, 2270) * mm, "radius": 13.5 * mm});
            skCircle(sketch, "E179", {"center": v(110.38, 2270) * mm, "radius": 13.5 * mm});
            skCircle(sketch, "E180", {"center": v(309.12, 2270) * mm, "radius": 13.5 * mm});
            skSolve(sketch);
        }
        {
            var Q0;
            Q0=makeQuery(id+"F44.imprint","IMPRINT",FACE,{"disambiguationData":[TD([[makeQuery(id+"F44.imprint","IMPRINT",EDGE,{"derivedFrom":sQuery(id+"F44.wireOp",EDGE,"E177")}),1.0]])]});
            var Q1;
            Q1=makeQuery(id+"F44.imprint","IMPRINT",FACE,{"disambiguationData":[TD([[makeQuery(id+"F44.imprint","IMPRINT",EDGE,{"derivedFrom":sQuery(id+"F44.wireOp",EDGE,"E178")}),1.0]])]});
            var Q2;
            Q2=makeQuery(id+"F44.imprint","IMPRINT",FACE,{"disambiguationData":[TD([[makeQuery(id+"F44.imprint","IMPRINT",EDGE,{"derivedFrom":sQuery(id+"F44.wireOp",EDGE,"E179")}),1.0]])]});
            var Q3;
            Q3=makeQuery(id+"F44.imprint","IMPRINT",FACE,{"disambiguationData":[TD([[makeQuery(id+"F44.imprint","IMPRINT",EDGE,{"derivedFrom":sQuery(id+"F44.wireOp",EDGE,"E180")}),1.0]])]});
            var Q4;
            Q4=makeQuery(id+"F44.imprint","IMPRINT",FACE,{"disambiguationData":[TD([[makeQuery(id+"F44.imprint","IMPRINT",EDGE,{"derivedFrom":sQuery(id+"F44.wireOp",EDGE,"E173")}),1.0]])]});
            var Q5;
            Q5=makeQuery(id+"F44.imprint","IMPRINT",FACE,{"disambiguationData":[TD([[makeQuery(id+"F44.imprint","IMPRINT",EDGE,{"derivedFrom":sQuery(id+"F44.wireOp",EDGE,"E174")}),1.0]])]});
            var Q6;
            Q6=makeQuery(id+"F44.imprint","IMPRINT",FACE,{"disambiguationData":[TD([[makeQuery(id+"F44.imprint","IMPRINT",EDGE,{"derivedFrom":sQuery(id+"F44.wireOp",EDGE,"E175")}),1.0]])]});
            var Q7;
            Q7=makeQuery(id+"F44.imprint","IMPRINT",FACE,{"disambiguationData":[TD([[makeQuery(id+"F44.imprint","IMPRINT",EDGE,{"derivedFrom":sQuery(id+"F44.wireOp",EDGE,"E176")}),1.0]])]});
            var Q8;
            Q8=makeQuery(id+"F44.imprint","IMPRINT",FACE,{"disambiguationData":[TD([[makeQuery(id+"F44.imprint","IMPRINT",EDGE,{"derivedFrom":sQuery(id+"F44.wireOp",EDGE,"E169")}),1.0]])]});
            var Q9;
            Q9=makeQuery(id+"F44.imprint","IMPRINT",FACE,{"disambiguationData":[TD([[makeQuery(id+"F44.imprint","IMPRINT",EDGE,{"derivedFrom":sQuery(id+"F44.wireOp",EDGE,"E168")}),1.0]])]});
            var Q10;
            Q10=makeQuery(id+"F44.imprint","IMPRINT",FACE,{"disambiguationData":[TD([[makeQuery(id+"F44.imprint","IMPRINT",EDGE,{"derivedFrom":sQuery(id+"F44.wireOp",EDGE,"E170")}),1.0]])]});
            var Q11;
            Q11=makeQuery(id+"F44.imprint","IMPRINT",FACE,{"disambiguationData":[TD([[makeQuery(id+"F44.imprint","IMPRINT",EDGE,{"derivedFrom":sQuery(id+"F44.wireOp",EDGE,"E171")}),1.0]])]});
            var Q12;
            Q12=makeQuery(id+"F44.imprint","IMPRINT",FACE,{"disambiguationData":[TD([[makeQuery(id+"F44.imprint","IMPRINT",EDGE,{"derivedFrom":sQuery(id+"F44.wireOp",EDGE,"E166.MirrorC")}),-1.0]])]});
            var Q13;
            Q13=makeQuery(id+"F44.imprint","IMPRINT",FACE,{"disambiguationData":[TD([[makeQuery(id+"F44.imprint","IMPRINT",EDGE,{"derivedFrom":sQuery(id+"F44.wireOp",EDGE,"E161")}),1.0]])]});
            var Q14;
            Q14=makeQuery(id+"F44.imprint","IMPRINT",FACE,{"disambiguationData":[TD([[makeQuery(id+"F44.imprint","IMPRINT",EDGE,{"derivedFrom":sQuery(id+"F44.wireOp",EDGE,"E163.MirrorC")}),-1.0]])]});
            var Q15;
            Q15=makeQuery(id+"F44.imprint","IMPRINT",FACE,{"disambiguationData":[TD([[makeQuery(id+"F44.imprint","IMPRINT",EDGE,{"derivedFrom":sQuery(id+"F44.wireOp",EDGE,"E167.MirrorC")}),1.0]])]});
            extrude(context, id + "F45", {"entities" : qUnion([Q0, Q1, Q2, Q3, Q4, Q5, Q6, Q7, Q8, Q9, Q10, Q11, Q12, Q13, Q14, Q15]), "operationType" : NewBodyOperationType.REMOVE, "oppositeDirection" : true, "depth" : 25 * mm});
        }
    });
